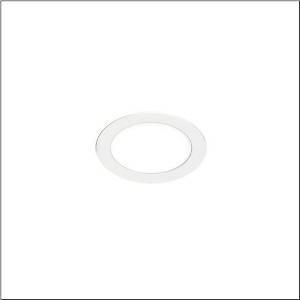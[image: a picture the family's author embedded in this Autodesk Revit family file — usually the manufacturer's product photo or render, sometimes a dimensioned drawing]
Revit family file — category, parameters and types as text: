
# Revit family: lunis_41_flat_51dr10mdgbb
name_source: partatom
category: Lighting Fixtures
units: mm (PartAtom-declared; Revit-internal decimal feet)

## family parameters
Cut with Voids When Loaded = No
Host = Face
Light Source = No
Part Type = Normal
Room Calculation Point = No
Round Connector Dimension = Use Diameter
Shared = No

## types (1)
- --- (1 x LED, 1580 lm, 12.5 W, 4000K)
    Apparent Load = 13 VA
    CIE Flux Codes = 49 80 96 100 100
    Color Rendering = 80
    Color Temperature = 4000K
    Default Elevation = 1800 mm
    Description = Lunis 41,  Flat, downlight, light emission: direct distribution, LED rated luminous flux: 1.530lm, light colour: 830/840, mains connection: 230V, AC, 50/60Hz, housing, round, of aluminium, coated, traffic white (RAL 9016), diameter: 170mm, protection rating (complete): IP20, protection rating (on room side): IP44, insulation class (complete): insulation class II (safety insulation), certification: CE, permissible ambient temperature for indoor applications: -20..+40°C, packaging unit: 1 piece
    Height = 0 mm  [stored 0 ft]
    Lamp = 1 x LED
    Lamp Light Flux = 1580 lm
    Lamp Power = 12.5 W
    Lamp count = 1
    Length = 170 mm  [stored 0.557743 ft]
    Luminous efficacy = 126 lm/W
    Manufacturer = Siteco
    ModVariant = No
    Model = 51DR10MDGBB
    Mounting Place = Ceiling
    Mounting Type = Recessed
    Number of Poles = 1
    OnlyDefault = Yes
    Power Factor = 1
    Product Name = Lunis 41 Flat
    Product group = downlight
    ProductGroupID = 401
    Protection Class = Protection class II
    Protection Degree = IP 20
    RLX_Detail_Level = 1
    RLX_Emergency_Light_Flux = 0 lm
    RLX_Emergency_Type = 0
    RLX_Emergency_Type_DB = No
    RlxData = <blob elided: 9773 chars, md5=4cc505c8>
    Socket = socket
    Standby Power = 0 W
    System Light Flux = 1580 lm
    System Power = 13 W
    Type Comments = factory setting: colour temperature 4000K
    Type Image = l_1340921.jpg
    URL = http://relux.com
    VarID = @adj_002227
    Voltage = 0 V
    Weight = 0.00 kg
    Width = 0 mm  [stored 0 ft]

note: [stored X ft] marks values corroborated as IEEE doubles in the binary element streams (Revit-internal decimal feet)

## geometry (parser evidence)
native form markers: Sweep x8
no freeform markers — native parametric forms only
